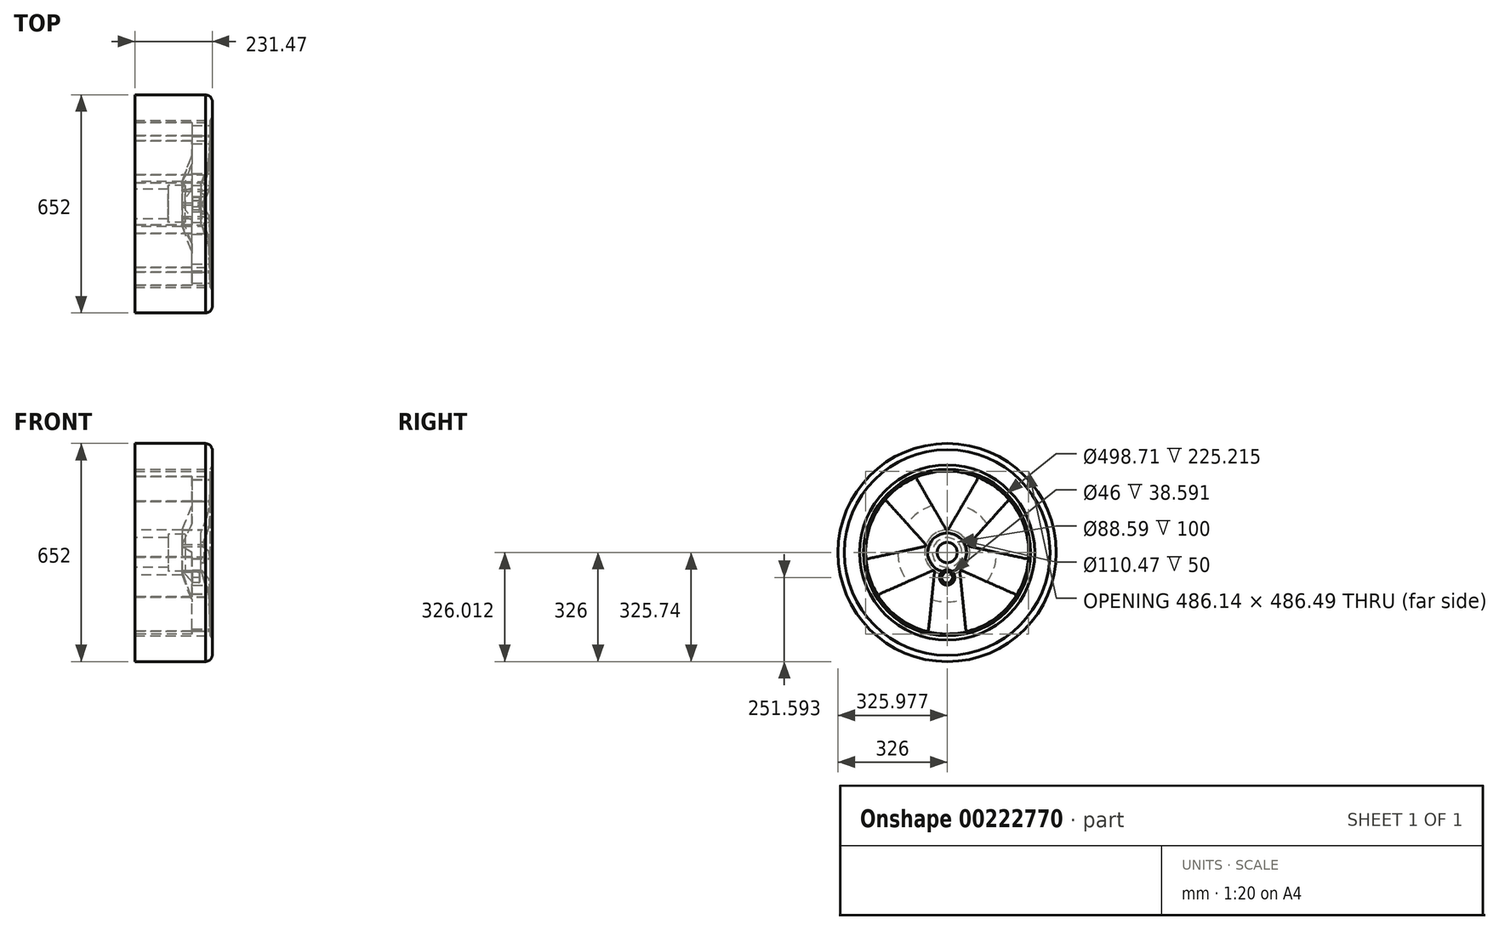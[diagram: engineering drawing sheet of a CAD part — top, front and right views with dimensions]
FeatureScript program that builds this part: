
annotation { "Feature Type Name" : "Feature", "Feature Type Description" : "" }
export const myFeature = defineFeature(function(context is Context, id is Id, definition is map)
    precondition{}
    {
        {
            var Q0;
            Q0=qCreatedBy(makeId("Front.planeOp"),FACE);
            var sketch = newSketch(context, id + "F0", { "sketchPlane" : qUnion([Q0])});
            skLineSegment(sketch, "E0", {"start": v(28, 191.01) * mm, "end": v(0, 191.01) * mm});
            skLineSegment(sketch, "E1", {"start": v(0, 191.01) * mm, "end": v(-87.05, 191.01) * mm});
            skLineSegment(sketch, "E2", {"start": v(-87.05, 191.01) * mm, "end": v(-87.05, 0) * mm});
            skLineSegment(sketch, "E3", {"start": v(-87.05, 0) * mm, "end": v(0, 0) * mm});
            skLineSegment(sketch, "E4", {"start": v(0, 0) * mm, "end": v(1, 0) * mm});
            skPoint(sketch, "E5.start.orphan", {"position": v(23, -2.12) * mm});
            skPoint(sketch, "E6.start.orphan", {"position": v(28, 0) * mm});
            skLineSegment(sketch, "E7", {"start": v(0, 0) * mm, "end": v(0, -23.19) * mm});
            skLineSegment(sketch, "E8", {"start": v(5, -28.19) * mm, "end": v(8.22, -28.19) * mm});
            skLineSegment(sketch, "E9", {"start": v(10.22, -30.19) * mm, "end": v(10.22, -58.34) * mm});
            skLineSegment(sketch, "E10", {"start": v(10.22, -58.34) * mm, "end": v(-87.05, -58.34) * mm});
            skLineSegment(sketch, "E11", {"start": v(-87.05, -58.34) * mm, "end": v(-87.05, 0) * mm});
            skPoint(sketch, "E12.visualSharp", {"position": v(0, -28.19) * mm});
            skArc(sketch, "E12.filletArc", {"start": v(0, -23.19) * mm, "mid": v(1.46, -26.72) * mm, "end": v(5, -28.19) * mm});
            skPoint(sketch, "E13.visualSharp", {"position": v(10.22, -28.19) * mm});
            skArc(sketch, "E13.filletArc", {"start": v(10.22, -30.19) * mm, "mid": v(9.63, -28.77) * mm, "end": v(8.22, -28.19) * mm});
            skPoint(sketch, "E14.visualSharp", {"position": v(23, 66.11) * mm});
            skLineSegment(sketch, "E15", {"start": v(28, 191.01) * mm, "end": v(28, 184.92) * mm});
            skLineSegment(sketch, "E16", {"start": v(28, 184.92) * mm, "end": v(23, 66.11) * mm});
            skLineSegment(sketch, "E17", {"start": v(23, 66.11) * mm, "end": v(0, 0) * mm});
            skLineSegment(sketch, "E18", {"start": v(28, 191.01) * mm, "end": v(34.26, 203.1) * mm});
            skLineSegment(sketch, "E19", {"start": v(34.26, 203.1) * mm, "end": v(34.26, 248.89) * mm});
            skLineSegment(sketch, "E20", {"start": v(13.81, 267.66) * mm, "end": v(-87.05, 267.66) * mm});
            skLineSegment(sketch, "E21", {"start": v(-87.05, 267.66) * mm, "end": v(-87.05, 191.01) * mm});
            skFitSpline(sketch, "E22", {"points": [v(13.81, 267.66) * mm, v(27.82, 262.23) * mm, v(34.26, 248.89) * mm], "startDerivative": vector(31.68, -6.82) * mm, "endDerivative": vector(9.2, -30.75) * mm});
            skLineSegment(sketch, "E23", {"start": v(28, 191.01) * mm, "end": v(-197.21, 191.01) * mm});
            skLineSegment(sketch, "E24", {"start": v(-197.21, 191.01) * mm, "end": v(-197.21, -58.34) * mm});
            skLineSegment(sketch, "E25", {"start": v(-197.21, -58.34) * mm, "end": v(-87.05, -58.34) * mm});
            skLineSegment(sketch, "E26", {"start": v(-197.21, 191.01) * mm, "end": v(-197.21, 267.66) * mm});
            skLineSegment(sketch, "E27", {"start": v(-197.21, 267.66) * mm, "end": v(-87.05, 267.66) * mm});
            skSolve(sketch);
        }
        {
            var Q0;
            Q0=makeQuery(id+"F0.imprint","IMPRINT",FACE,{"disambiguationData":[TD([[makeQuery(id+"F0.imprint","IMPRINT",EDGE,{"derivedFrom":sQuery(id+"F0.wireOp",EDGE,"E3")}),-1.0]])]});
            var Q1;
            {var subQ1=sQuery(id+"F0.wireOp",EDGE,"E2");Q1=makeQuery(id+"F0.imprint","IMPRINT",FACE,{"disambiguationData":[TD([[makeQuery(id+"F0.imprint","IMPRINT",EDGE,{"derivedFrom":subQ1}),1.0]])]});}
            var Q2;
            {var subQ2=sQuery(id+"F0.wireOp",EDGE,"E2");Q2=makeQuery(id+"F0.imprint","IMPRINT",FACE,{"disambiguationData":[TD([[makeQuery(id+"F0.imprint","IMPRINT",EDGE,{"derivedFrom":subQ2}),-1.0]])]});}
            var Q3;
            Q3=sQuery(id+"F0.wireOp",EDGE,"E10");
            revolve(context, id + "F1", {"entities" : qUnion([Q0, Q1, Q2]), "axis" : qUnion([Q3]), "revolveType" : RevolveType.FULL});
        }
        {
            var Q0;
            Q0=makeQuery(id+"F1.opRevolve","SWEPT_FACE",FACE,{"disambiguationData":[OSD([sQuery(id+"F0.wireOp",EDGE,"E15")])]});
            var sketch = newSketch(context, id + "F2", { "sketchPlane" : qUnion([Q0])});
            skPoint(sketch, "E28.start.orphan", {"position": v(0, 13.97) * mm});
            skLineSegment(sketch, "E29", {"start": v(3.37, 10.71) * mm, "end": v(89.53, 159.08) * mm});
            skLineSegment(sketch, "E30", {"start": v(-3.45, 10.85) * mm, "end": v(-90.5, 160.73) * mm});
            skPoint(sketch, "E31.orphan", {"position": v(0, 184.92) * mm});
            skArc(sketch, "E32", {"start": v(-3.75, 11.38) * mm, "mid": v(0.1, 9.03) * mm, "end": v(3.84, 11.53) * mm});
            skPoint(sketch, "E32.first.point", {"position": v(-3.45, 10.85) * mm});
            skPoint(sketch, "E32.second.point", {"position": v(3.37, 10.71) * mm});
            skPoint(sketch, "E32.third.point", {"position": v(1.3, 17.2) * mm});
            skArc(sketch, "E33", {"start": v(-86.67, 168.95) * mm, "mid": v(-90.7, 165.21) * mm, "end": v(-89.94, 159.77) * mm});
            skPoint(sketch, "E33.first.point", {"position": v(-89.94, 159.77) * mm});
            skPoint(sketch, "E33.second.point", {"position": v(-86.67, 168.95) * mm});
            skPoint(sketch, "E33.third.point", {"position": v(-79.18, 163.63) * mm});
            skArc(sketch, "E34", {"start": v(89.1, 158.32) * mm, "mid": v(90.16, 164.15) * mm, "end": v(86.68, 168.95) * mm});
            skPoint(sketch, "E34.first.point", {"position": v(89.1, 158.32) * mm});
            skPoint(sketch, "E34.second.point", {"position": v(86.68, 168.95) * mm});
            skPoint(sketch, "E34.third.point", {"position": v(77.18, 167.5) * mm});
            skSolve(sketch);
        }
        {
            var Q0;
            Q0=makeQuery(id+"F1.opRevolve","SWEPT_EDGE",EDGE,{"disambiguationData":[OSD([sQuery(id+"F0.wireOp",EDGE,"E16"),sQuery(id+"F0.wireOp",EDGE,"E17")])]});
            fillet(context, id + "F3", {"entities" : qUnion([Q0]), "radius" : 100 * mm, "allowEdgeOverflow" : false});
        }
        {
            var Q0;
            {var subQ5=sQuery(id+"F2.wireOp",EDGE,"E29");var subQ7=sQuery(id+"F2.wireOp",EDGE,"E32");var subQ8=makeQuery(id+"F2.imprint","INTERSECT",VERTEX,{"disambiguationData":[OD(0.0)],"derivedFrom":[subQ5,subQ7]});Q0=makeQuery(id+"F2.imprint","IMPRINT",FACE,{"disambiguationData":[TD([[makeQuery(id+"F2.imprint","IMPRINT",EDGE,{"disambiguationData":[TD([[subQ8,-1.0]])],"derivedFrom":subQ5}),1.0]])]});}
            extrude(context, id + "F4", {"entities" : qUnion([Q0]), "oppositeDirection" : true, "depth" : 260 * mm});
        }
        {
            var Q0;
            Q0=makeQuery(id+"F4.opExtrude","SWEPT_BODY",BODY,{"disambiguationData":[OSD([sQuery(id+"F0.wireOp",EDGE,"E15"),sQuery(id+"F0.wireOp",EDGE,"E16"),sQuery(id+"F2.wireOp",EDGE,"E29"),sQuery(id+"F2.wireOp",EDGE,"E30"),sQuery(id+"F2.wireOp",EDGE,"E32"),sQuery(id+"F2.wireOp",EDGE,"E33"),sQuery(id+"F2.wireOp",EDGE,"E34")])]});
            var Q1;
            Q1=makeQuery(id+"F1.opRevolve","SWEPT_EDGE",EDGE,{"disambiguationData":[OSD([sQuery(id+"F0.wireOp",EDGE,"E3"),sQuery(id+"F0.wireOp",EDGE,"E7"),sQuery(id+"F0.wireOp",EDGE,"E17")])]});
            circularPattern(context, id + "F5", {"entities" : qUnion([Q0]), "axis" : qUnion([Q1]), "angle" : 360 * degree, "instanceCount" : 5, "equalSpace" : true});
        }
        {
            var Q0;
            Q0=makeQuery(id+"F4.opExtrude","SWEPT_BODY",BODY,{"disambiguationData":[OSD([sQuery(id+"F0.wireOp",EDGE,"E15"),sQuery(id+"F0.wireOp",EDGE,"E16"),sQuery(id+"F2.wireOp",EDGE,"E29"),sQuery(id+"F2.wireOp",EDGE,"E30"),sQuery(id+"F2.wireOp",EDGE,"E32"),sQuery(id+"F2.wireOp",EDGE,"E33"),sQuery(id+"F2.wireOp",EDGE,"E34")])]});
            var Q1;
            Q1=makeQuery(id+"F5.opPattern","COPY",BODY,{"derivedFrom":makeQuery(id+"F4.opExtrude","SWEPT_BODY",BODY,{"disambiguationData":[OSD([sQuery(id+"F0.wireOp",EDGE,"E15"),sQuery(id+"F0.wireOp",EDGE,"E16"),sQuery(id+"F2.wireOp",EDGE,"E29"),sQuery(id+"F2.wireOp",EDGE,"E30"),sQuery(id+"F2.wireOp",EDGE,"E32"),sQuery(id+"F2.wireOp",EDGE,"E33"),sQuery(id+"F2.wireOp",EDGE,"E34")])]}),"instanceName":"4"});
            var Q2;
            Q2=makeQuery(id+"F5.opPattern","COPY",BODY,{"derivedFrom":makeQuery(id+"F4.opExtrude","SWEPT_BODY",BODY,{"disambiguationData":[OSD([sQuery(id+"F0.wireOp",EDGE,"E15"),sQuery(id+"F0.wireOp",EDGE,"E16"),sQuery(id+"F2.wireOp",EDGE,"E29"),sQuery(id+"F2.wireOp",EDGE,"E30"),sQuery(id+"F2.wireOp",EDGE,"E32"),sQuery(id+"F2.wireOp",EDGE,"E33"),sQuery(id+"F2.wireOp",EDGE,"E34")])]}),"instanceName":"3"});
            var Q3;
            Q3=makeQuery(id+"F5.opPattern","COPY",BODY,{"derivedFrom":makeQuery(id+"F4.opExtrude","SWEPT_BODY",BODY,{"disambiguationData":[OSD([sQuery(id+"F0.wireOp",EDGE,"E15"),sQuery(id+"F0.wireOp",EDGE,"E16"),sQuery(id+"F2.wireOp",EDGE,"E29"),sQuery(id+"F2.wireOp",EDGE,"E30"),sQuery(id+"F2.wireOp",EDGE,"E32"),sQuery(id+"F2.wireOp",EDGE,"E33"),sQuery(id+"F2.wireOp",EDGE,"E34")])]}),"instanceName":"2"});
            var Q4;
            Q4=makeQuery(id+"F5.opPattern","COPY",BODY,{"derivedFrom":makeQuery(id+"F4.opExtrude","SWEPT_BODY",BODY,{"disambiguationData":[OSD([sQuery(id+"F0.wireOp",EDGE,"E15"),sQuery(id+"F0.wireOp",EDGE,"E16"),sQuery(id+"F2.wireOp",EDGE,"E29"),sQuery(id+"F2.wireOp",EDGE,"E30"),sQuery(id+"F2.wireOp",EDGE,"E32"),sQuery(id+"F2.wireOp",EDGE,"E33"),sQuery(id+"F2.wireOp",EDGE,"E34")])]}),"instanceName":"1"});
            var Q5;
            Q5=makeQuery(id+"F1.opRevolve","SWEPT_BODY",BODY,{"disambiguationData":[OSD([sQuery(id+"F0.wireOp",EDGE,"E0"),sQuery(id+"F0.wireOp",EDGE,"E1"),sQuery(id+"F0.wireOp",EDGE,"E2"),sQuery(id+"F0.wireOp",EDGE,"E7"),sQuery(id+"F0.wireOp",EDGE,"E8"),sQuery(id+"F0.wireOp",EDGE,"E9"),sQuery(id+"F0.wireOp",EDGE,"E10"),sQuery(id+"F0.wireOp",EDGE,"E11"),sQuery(id+"F0.wireOp",EDGE,"E12.filletArc"),sQuery(id+"F0.wireOp",EDGE,"E13.filletArc"),sQuery(id+"F0.wireOp",EDGE,"E15"),sQuery(id+"F0.wireOp",EDGE,"E16"),sQuery(id+"F0.wireOp",EDGE,"E17")])]});
            booleanBodies(context, id + "F6", {"operationType" : BooleanOperationType.SUBTRACTION, "tools" : qUnion([Q0, Q1, Q2, Q3, Q4]), "targets" : qUnion([Q5])});
        }
        {
            var Q0;
            Q0=makeQuery(id+"F1.opRevolve","SWEPT_FACE",FACE,{"disambiguationData":[OSD([sQuery(id+"F0.wireOp",EDGE,"E7")])]});
            var sketch = newSketch(context, id + "F7", { "sketchPlane" : qUnion([Q0])});
            skLineSegment(sketch, "E35", {"start": v(0, -116.68) * mm, "end": v(0, -109.75) * mm});
            skLineSegment(sketch, "E36", {"start": v(0, -109.75) * mm, "end": v(0, -132.75) * mm});
            skPoint(sketch, "E36.endSnap0", {"position": v(0, -113.21) * mm});
            skCircle(sketch, "E37", {"center": v(0, -132.75) * mm, "radius": 23 * mm});
            skSolve(sketch);
        }
        {
            var Q0;
            Q0=qSketchRegion(id+"F7",true);
            extrude(context, id + "F8", {"entities" : qUnion([Q0]), "operationType" : NewBodyOperationType.REMOVE, "endBound" : BoundingType.SYMMETRIC, "oppositeDirection" : true, "depth" : 50 * mm});
        }
        {
            var Q0;
            Q0=makeQuery(id+"F8.boolean.opBoolean","COPY",FACE,{"derivedFrom":makeQuery(id+"F8.opExtrude","CAP_FACE",FACE,{"disambiguationData":[OSD([sQuery(id+"F7.wireOp",EDGE,"E37")])],"isStart":false})});
            var sketch = newSketch(context, id + "F9", { "sketchPlane" : qUnion([Q0])});
            skLineSegment(sketch, "E38.0", {"start": v(8.87, -116.92) * mm, "end": v(18.14, -132.52) * mm});
            skLineSegment(sketch, "E38.1", {"start": v(18.14, -132.52) * mm, "end": v(9.27, -148.34) * mm});
            skLineSegment(sketch, "E38.2", {"start": v(9.27, -148.34) * mm, "end": v(-8.87, -148.58) * mm});
            skLineSegment(sketch, "E38.3", {"start": v(-8.87, -148.58) * mm, "end": v(-18.14, -132.98) * mm});
            skLineSegment(sketch, "E38.4", {"start": v(-18.14, -132.98) * mm, "end": v(-9.27, -117.15) * mm});
            skLineSegment(sketch, "E38.5", {"start": v(-9.27, -117.15) * mm, "end": v(8.87, -116.92) * mm});
            skPoint(sketch, "E39.center.orphan", {"position": v(0, -132.75) * mm});
            skSolve(sketch);
        }
        {
            var Q0;
            Q0=makeQuery(id+"F9.imprint","IMPRINT",FACE,{"disambiguationData":[TD([[makeQuery(id+"F9.imprint","IMPRINT",EDGE,{"derivedFrom":sQuery(id+"F9.wireOp",EDGE,"E38.0")}),-1.0]])]});
            extrude(context, id + "F10", {"entities" : qUnion([Q0]), "operationType" : NewBodyOperationType.ADD, "depth" : 21 * mm});
        }
        {
            var Q0;
            Q0=makeQuery(id+"F10.opExtrude","CAP_EDGE",EDGE,{"disambiguationData":[OSD([sQuery(id+"F9.wireOp",EDGE,"E38.5")])],"isStart":false});
            var Q1;
            Q1=makeQuery(id+"F10.opExtrude","CAP_EDGE",EDGE,{"disambiguationData":[OSD([sQuery(id+"F9.wireOp",EDGE,"E38.0")])],"isStart":false});
            var Q2;
            Q2=makeQuery(id+"F10.opExtrude","CAP_EDGE",EDGE,{"disambiguationData":[OSD([sQuery(id+"F9.wireOp",EDGE,"E38.1")])],"isStart":false});
            var Q3;
            Q3=makeQuery(id+"F10.opExtrude","CAP_EDGE",EDGE,{"disambiguationData":[OSD([sQuery(id+"F9.wireOp",EDGE,"E38.2")])],"isStart":false});
            var Q4;
            Q4=makeQuery(id+"F10.opExtrude","CAP_EDGE",EDGE,{"disambiguationData":[OSD([sQuery(id+"F9.wireOp",EDGE,"E38.3")])],"isStart":false});
            var Q5;
            Q5=makeQuery(id+"F10.opExtrude","CAP_EDGE",EDGE,{"disambiguationData":[OSD([sQuery(id+"F9.wireOp",EDGE,"E38.4")])],"isStart":false});
            var Q6;
            Q6=makeQuery(id+"F2OYmmZjbPNK6g8_1.4.F10.opExtrude","CAP_FACE",FACE,{"disambiguationData":[OSD([sQuery(id+"F9.wireOp",EDGE,"E38.0"),sQuery(id+"F9.wireOp",EDGE,"E38.1"),sQuery(id+"F9.wireOp",EDGE,"E38.2"),sQuery(id+"F9.wireOp",EDGE,"E38.3"),sQuery(id+"F9.wireOp",EDGE,"E38.4"),sQuery(id+"F9.wireOp",EDGE,"E38.5")])],"isStart":false});
            var Q7;
            Q7=makeQuery(id+"F2OYmmZjbPNK6g8_1.1.F10.opExtrude","CAP_FACE",FACE,{"disambiguationData":[OSD([sQuery(id+"F9.wireOp",EDGE,"E38.0"),sQuery(id+"F9.wireOp",EDGE,"E38.1"),sQuery(id+"F9.wireOp",EDGE,"E38.2"),sQuery(id+"F9.wireOp",EDGE,"E38.3"),sQuery(id+"F9.wireOp",EDGE,"E38.4"),sQuery(id+"F9.wireOp",EDGE,"E38.5")])],"isStart":false});
            var Q8;
            Q8=makeQuery(id+"F2OYmmZjbPNK6g8_1.2.F10.opExtrude","CAP_FACE",FACE,{"disambiguationData":[OSD([sQuery(id+"F9.wireOp",EDGE,"E38.0"),sQuery(id+"F9.wireOp",EDGE,"E38.1"),sQuery(id+"F9.wireOp",EDGE,"E38.2"),sQuery(id+"F9.wireOp",EDGE,"E38.3"),sQuery(id+"F9.wireOp",EDGE,"E38.4"),sQuery(id+"F9.wireOp",EDGE,"E38.5")])],"isStart":false});
            var Q9;
            Q9=makeQuery(id+"F2OYmmZjbPNK6g8_1.3.F10.opExtrude","CAP_FACE",FACE,{"disambiguationData":[OSD([sQuery(id+"F9.wireOp",EDGE,"E38.0"),sQuery(id+"F9.wireOp",EDGE,"E38.1"),sQuery(id+"F9.wireOp",EDGE,"E38.2"),sQuery(id+"F9.wireOp",EDGE,"E38.3"),sQuery(id+"F9.wireOp",EDGE,"E38.4"),sQuery(id+"F9.wireOp",EDGE,"E38.5")])],"isStart":false});
            fillet(context, id + "F11", {"entities" : qUnion([Q0, Q1, Q2, Q3, Q4, Q5, Q6, Q7, Q8, Q9]), "radius" : 2 * mm, "tangentPropagation" : true, "allowEdgeOverflow" : false});
        }
        {
            var Q0;
            Q0=makeQuery(id+"F1.opRevolve","SWEPT_FACE",FACE,{"disambiguationData":[OSD([sQuery(id+"F0.wireOp",EDGE,"E24"),sQuery(id+"F0.wireOp",EDGE,"E26")])]});
            var sketch = newSketch(context, id + "F12", { "sketchPlane" : qUnion([Q0])});
            skCircle(sketch, "E40", {"center": v(0, -58.34) * mm, "radius": 44.3 * mm});
            skSolve(sketch);
        }
        {
            var Q0;
            Q0=qSketchRegion(id+"F12",true);
            extrude(context, id + "F13", {"entities" : qUnion([Q0]), "operationType" : NewBodyOperationType.REMOVE, "oppositeDirection" : true, "depth" : 150 * mm});
        }
        {
            var Q0;
            Q0=makeQuery(id+"F13.boolean.opBoolean","COPY",FACE,{"derivedFrom":makeQuery(id+"F13.opExtrude","CAP_FACE",FACE,{"disambiguationData":[OSD([sQuery(id+"F12.wireOp",EDGE,"E40")])],"isStart":false})});
            cPlane(context, id + "F14", {"entities" : qUnion([Q0]), "cplaneType" : CPlaneType.OFFSET, "offset" : 50 * mm, "width" : 150 * mm, "height" : 150 * mm});
        }
        {
            var Q0;
            Q0=qCreatedBy(id+"F14.planeOp",FACE);
            var sketch = newSketch(context, id + "F15", { "sketchPlane" : qUnion([Q0])});
            skCircle(sketch, "E41", {"center": v(0, -58.6) * mm, "radius": 55.23 * mm});
            skSolve(sketch);
        }
        {
            var Q0;
            Q0=qSketchRegion(id+"F15",true);
            extrude(context, id + "F16", {"entities" : qUnion([Q0]), "operationType" : NewBodyOperationType.REMOVE, "oppositeDirection" : true, "depth" : 50 * mm});
        }
        {
            var Q0;
            Q0=makeQuery(id+"F1.opRevolve","SWEPT_FACE",FACE,{"disambiguationData":[OSD([sQuery(id+"F0.wireOp",EDGE,"E24"),sQuery(id+"F0.wireOp",EDGE,"E26")])]});
            var sketch = newSketch(context, id + "F17", { "sketchPlane" : qUnion([Q0])});
            skCircle(sketch, "E42", {"center": v(0, -58.34) * mm, "radius": 67.37 * mm});
            skCircle(sketch, "E43", {"center": v(0, -58.34) * mm, "radius": 243.23 * mm});
            skSolve(sketch);
        }
        {
            var Q0;
            {var subQ0=makeQuery(id+"F1.opRevolve","SWEPT_FACE",FACE,{"disambiguationData":[OSD([sQuery(id+"F0.wireOp",EDGE,"E24")])]});var subQ2=makeQuery(id+"F6.opBoolean","INTERSECT",EDGE,{"derivedFrom":[subQ0,makeQuery(id+"F4.opExtrude","SWEPT_FACE",FACE,{"disambiguationData":[OSD([sQuery(id+"F2.wireOp",EDGE,"E29")])]})]});Q0=makeQuery(id+"F17.imprint","IMPRINT",FACE,{"disambiguationData":[TD([[makeQuery(id+"F17.imprint","IMPRINT",EDGE,{"derivedFrom":subQ2}),-1.0]])]});}
            var Q1;
            {var subQ0=makeQuery(id+"F1.opRevolve","SWEPT_FACE",FACE,{"disambiguationData":[OSD([sQuery(id+"F0.wireOp",EDGE,"E24")])]});var subQ2=makeQuery(id+"F6.opBoolean","INTERSECT",EDGE,{"derivedFrom":[subQ0,makeQuery(id+"F5.opPattern","COPY",FACE,{"derivedFrom":makeQuery(id+"F4.opExtrude","SWEPT_FACE",FACE,{"disambiguationData":[OSD([sQuery(id+"F2.wireOp",EDGE,"E30")])]}),"instanceName":"1"})]});Q1=makeQuery(id+"F17.imprint","IMPRINT",FACE,{"disambiguationData":[TD([[makeQuery(id+"F17.imprint","IMPRINT",EDGE,{"derivedFrom":subQ2}),1.0]])]});}
            var Q2;
            {var subQ0=makeQuery(id+"F1.opRevolve","SWEPT_FACE",FACE,{"disambiguationData":[OSD([sQuery(id+"F0.wireOp",EDGE,"E24")])]});var subQ7=makeQuery(id+"F6.opBoolean","INTERSECT",EDGE,{"derivedFrom":[subQ0,makeQuery(id+"F5.opPattern","COPY",FACE,{"derivedFrom":makeQuery(id+"F4.opExtrude","SWEPT_FACE",FACE,{"disambiguationData":[OSD([sQuery(id+"F2.wireOp",EDGE,"E30")])]}),"instanceName":"2"})]});Q2=makeQuery(id+"F17.imprint","IMPRINT",FACE,{"disambiguationData":[TD([[makeQuery(id+"F17.imprint","IMPRINT",EDGE,{"derivedFrom":subQ7}),1.0]])]});}
            var Q3;
            {var subQ0=makeQuery(id+"F1.opRevolve","SWEPT_FACE",FACE,{"disambiguationData":[OSD([sQuery(id+"F0.wireOp",EDGE,"E24")])]});var subQ1=makeQuery(id+"F6.opBoolean","INTERSECT",EDGE,{"derivedFrom":[subQ0,makeQuery(id+"F5.opPattern","COPY",FACE,{"derivedFrom":makeQuery(id+"F4.opExtrude","SWEPT_FACE",FACE,{"disambiguationData":[OSD([sQuery(id+"F2.wireOp",EDGE,"E30")])]}),"instanceName":"3"})]});Q3=makeQuery(id+"F17.imprint","IMPRINT",FACE,{"disambiguationData":[TD([[makeQuery(id+"F17.imprint","IMPRINT",EDGE,{"derivedFrom":subQ1}),1.0]])]});}
            var Q4;
            {var subQ0=makeQuery(id+"F1.opRevolve","SWEPT_FACE",FACE,{"disambiguationData":[OSD([sQuery(id+"F0.wireOp",EDGE,"E24")])]});var subQ5=makeQuery(id+"F6.opBoolean","INTERSECT",EDGE,{"derivedFrom":[subQ0,makeQuery(id+"F4.opExtrude","SWEPT_FACE",FACE,{"disambiguationData":[OSD([sQuery(id+"F2.wireOp",EDGE,"E30")])]})]});Q4=makeQuery(id+"F17.imprint","IMPRINT",FACE,{"disambiguationData":[TD([[makeQuery(id+"F17.imprint","IMPRINT",EDGE,{"derivedFrom":subQ5}),1.0]])]});}
            extrude(context, id + "F18", {"entities" : qUnion([Q0, Q1, Q2, Q3, Q4]), "operationType" : NewBodyOperationType.REMOVE, "oppositeDirection" : true, "depth" : 171 * mm});
        }
        {
            var Q0;
            {var subQ0=sQuery(id+"F17.wireOp",EDGE,"E42");var subQ1=makeQuery(id+"F4.opExtrude","SWEPT_FACE",FACE,{"disambiguationData":[OSD([sQuery(id+"F2.wireOp",EDGE,"E32")])]});var subQ2=makeQuery(id+"F1.opRevolve","SWEPT_FACE",FACE,{"disambiguationData":[OSD([sQuery(id+"F0.wireOp",EDGE,"E24"),sQuery(id+"F0.wireOp",EDGE,"E26")])]});Q0=makeQuery(id+"F18.boolean.opBoolean","COPY",EDGE,{"derivedFrom":makeQuery(id+"F18.opExtrude","CAP_EDGE",EDGE,{"disambiguationData":[OSD([subQ0]),TDD([makeQuery(id+"F17.imprint","IMPRINT",EDGE,{"disambiguationData":[TD([[makeQuery(id+"F17.imprint","INTERSECT",VERTEX,{"derivedFrom":[makeQuery(id+"F6.opBoolean","INTERSECT",EDGE,{"derivedFrom":[subQ2,makeQuery(id+"F5.opPattern","COPY",FACE,{"derivedFrom":subQ1,"instanceName":"4"})]}),subQ0]}),-1.0]])],"derivedFrom":subQ0})])],"isStart":false})});}
            chamfer(context, id + "F19", {"entities" : qUnion([Q0]), "chamferType" : ChamferType.TWO_OFFSETS, "width1" : 80 * mm, "oppositeDirection" : true, "width2" : 30 * mm, "tangentPropagation" : true});
        }
        {
            var Q0;
            {var subQ2=sQuery(id+"F0.wireOp",EDGE,"E18");Q0=makeQuery(id+"F0.imprint","IMPRINT",FACE,{"disambiguationData":[TD([[makeQuery(id+"F0.imprint","IMPRINT",EDGE,{"derivedFrom":subQ2}),1.0]])]});}
            var Q1;
            {var subQ0=sQuery(id+"F0.wireOp",EDGE,"E21");Q1=makeQuery(id+"F0.imprint","IMPRINT",FACE,{"disambiguationData":[TD([[makeQuery(id+"F0.imprint","IMPRINT",EDGE,{"derivedFrom":subQ0}),-1.0]])]});}
            var Q2;
            Q2=sQuery(id+"F0.wireOp",EDGE,"E10");
            revolve(context, id + "F20", {"entities" : qUnion([Q0, Q1]), "axis" : qUnion([Q2]), "revolveType" : RevolveType.FULL});
        }
    });
